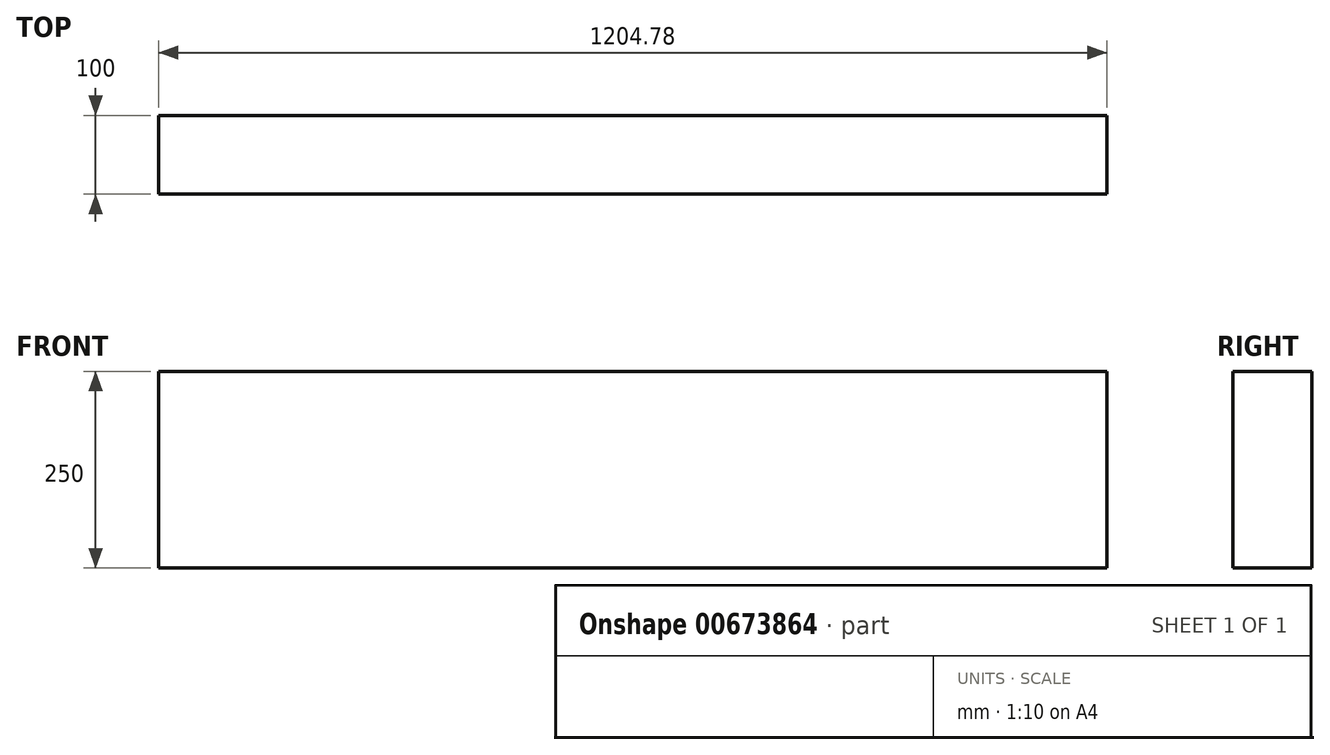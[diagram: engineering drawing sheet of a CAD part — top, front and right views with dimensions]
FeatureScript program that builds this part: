
annotation { "Feature Type Name" : "Feature", "Feature Type Description" : "" }
export const myFeature = defineFeature(function(context is Context, id is Id, definition is map)
    precondition{}
    {
        {
            var Q0;
            Q0=qCreatedBy(makeId("Front.planeOp"),FACE);
            var sketch = newSketch(context, id + "F0", { "sketchPlane" : qUnion([Q0])});
            skLineSegment(sketch, "E0", {"start": v(604.54, -102.51) * mm, "end": v(604.54, 147.49) * mm});
            skLineSegment(sketch, "E1.bottom", {"start": v(-600.24, 147.49) * mm, "end": v(604.54, 147.49) * mm});
            skLineSegment(sketch, "E1.top", {"start": v(-600.24, -102.51) * mm, "end": v(604.54, -102.51) * mm});
            skLineSegment(sketch, "E1.left", {"start": v(-600.24, 147.49) * mm, "end": v(-600.24, -102.51) * mm});
            skSolve(sketch);
        }
        {
            var Q0;
            Q0=makeQuery(id+"F0.imprint","IMPRINT",FACE,{"disambiguationData":[TD([[makeQuery(id+"F0.imprint","IMPRINT",EDGE,{"derivedFrom":sQuery(id+"F0.wireOp",EDGE,"E0")}),1.0]])]});
            extrude(context, id + "F1", {"entities" : qUnion([Q0]), "depth" : 100 * mm, "offsetDistance" : 25 * mm});
        }
    });
